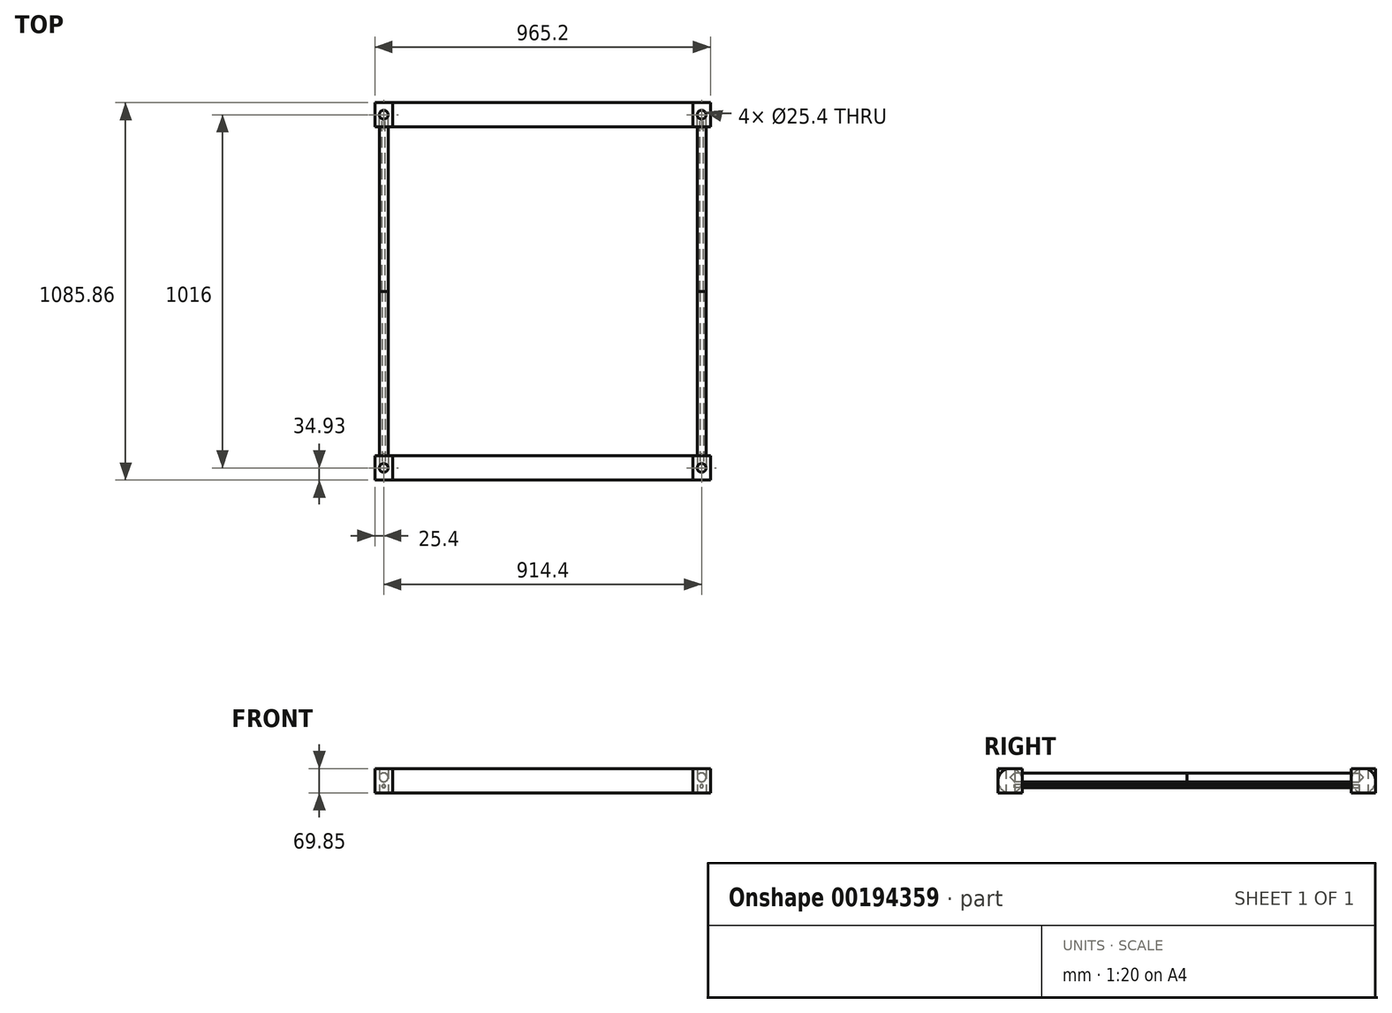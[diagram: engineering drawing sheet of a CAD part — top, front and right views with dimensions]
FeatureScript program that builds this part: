
annotation { "Feature Type Name" : "Feature", "Feature Type Description" : "" }
export const myFeature = defineFeature(function(context is Context, id is Id, definition is map)
    precondition{}
    {
        {
            var Q0;
            Q0=qCreatedBy(makeId("Front.planeOp"),FACE);
            var sketch = newSketch(context, id + "F0", { "sketchPlane" : qUnion([Q0])});
            skCircle(sketch, "E0", {"center": v(-457.2, 0) * mm, "radius": 12.7 * mm});
            skCircle(sketch, "E1", {"center": v(457.2, 0) * mm, "radius": 12.7 * mm});
            skLineSegment(sketch, "E2", {"start": v(-431.8, 25.4) * mm, "end": v(-482.6, 25.4) * mm});
            skLineSegment(sketch, "E3", {"start": v(-482.6, 25.4) * mm, "end": v(-482.6, -44.45) * mm});
            skLineSegment(sketch, "E4", {"start": v(-482.6, -44.45) * mm, "end": v(-431.8, -44.45) * mm});
            skLineSegment(sketch, "E5", {"start": v(482.6, -44.45) * mm, "end": v(482.6, 25.4) * mm});
            skLineSegment(sketch, "E6", {"start": v(482.6, 25.4) * mm, "end": v(431.8, 25.4) * mm});
            skCircle(sketch, "E7", {"center": v(-457.2, -25.4) * mm, "radius": 4.76 * mm});
            skCircle(sketch, "E8", {"center": v(457.2, -25.4) * mm, "radius": 4.76 * mm});
            skLineSegment(sketch, "E9", {"start": v(-431.8, 25.4) * mm, "end": v(-431.8, -44.45) * mm});
            skLineSegment(sketch, "E10", {"start": v(431.8, 25.4) * mm, "end": v(431.8, -44.45) * mm});
            skPoint(sketch, "E10.endSnap0", {"position": v(0, -44.45) * mm});
            skLineSegment(sketch, "E11", {"start": v(-431.8, -9.52) * mm, "end": v(431.8, -9.52) * mm});
            skPoint(sketch, "E12.orphan", {"position": v(0, 25.4) * mm});
            skLineSegment(sketch, "E13.trimOffspring", {"start": v(431.8, -44.45) * mm, "end": v(482.6, -44.45) * mm});
            skLineSegment(sketch, "E14", {"start": v(-431.8, 25.4) * mm, "end": v(431.8, 25.4) * mm});
            skSolve(sketch);
        }
        {
            var Q0;
            Q0=makeQuery(id+"F0.imprint","IMPRINT",FACE,{"disambiguationData":[TD([[makeQuery(id+"F0.imprint","IMPRINT",EDGE,{"derivedFrom":sQuery(id+"F0.wireOp",EDGE,"E1")}),-1.0]])]});
            var Q1;
            Q1=makeQuery(id+"F0.imprint","IMPRINT",FACE,{"disambiguationData":[TD([[makeQuery(id+"F0.imprint","IMPRINT",EDGE,{"derivedFrom":sQuery(id+"F0.wireOp",EDGE,"E0")}),1.0]])]});
            var Q2;
            Q2=makeQuery(id+"F0.imprint","IMPRINT",FACE,{"disambiguationData":[TD([[makeQuery(id+"F0.imprint","IMPRINT",EDGE,{"derivedFrom":sQuery(id+"F0.wireOp",EDGE,"E0")}),-1.0]])]});
            var Q3;
            Q3=makeQuery(id+"F0.imprint","IMPRINT",FACE,{"disambiguationData":[TD([[makeQuery(id+"F0.imprint","IMPRINT",EDGE,{"derivedFrom":sQuery(id+"F0.wireOp",EDGE,"E7")}),1.0]])]});
            var Q4;
            Q4=makeQuery(id+"F0.imprint","IMPRINT",FACE,{"disambiguationData":[TD([[makeQuery(id+"F0.imprint","IMPRINT",EDGE,{"derivedFrom":sQuery(id+"F0.wireOp",EDGE,"E1")}),1.0]])]});
            var Q5;
            Q5=makeQuery(id+"F0.imprint","IMPRINT",FACE,{"disambiguationData":[TD([[makeQuery(id+"F0.imprint","IMPRINT",EDGE,{"derivedFrom":sQuery(id+"F0.wireOp",EDGE,"E8")}),1.0]])]});
            extrude(context, id + "F1", {"entities" : qUnion([Q0, Q1, Q2, Q3, Q4, Q5]), "endBound" : BoundingType.SYMMETRIC, "oppositeDirection" : true, "depth" : 69.85 * mm});
        }
        {
            var Q0;
            {var subQ2=sQuery(id+"F0.wireOp",EDGE,"E11");Q0=makeQuery(id+"F0.imprint","IMPRINT",FACE,{"disambiguationData":[TD([[makeQuery(id+"F0.imprint","IMPRINT",EDGE,{"derivedFrom":subQ2}),1.0]])]});}
            var Q1;
            Q1=sQuery(id+"F0.wireOp",EDGE,"E11");
            revolve(context, id + "F2", {"entities" : qUnion([Q0]), "axis" : qUnion([Q1]), "revolveType" : RevolveType.FULL});
        }
        {
            var Q0;
            Q0=makeQuery(id+"F0.imprint","IMPRINT",FACE,{"disambiguationData":[TD([[makeQuery(id+"F0.imprint","IMPRINT",EDGE,{"derivedFrom":sQuery(id+"F0.wireOp",EDGE,"E1")}),1.0]])]});
            var Q1;
            Q1=makeQuery(id+"F0.imprint","IMPRINT",FACE,{"disambiguationData":[TD([[makeQuery(id+"F0.imprint","IMPRINT",EDGE,{"derivedFrom":sQuery(id+"F0.wireOp",EDGE,"E8")}),1.0]])]});
            var Q2;
            Q2=makeQuery(id+"F0.imprint","IMPRINT",FACE,{"disambiguationData":[TD([[makeQuery(id+"F0.imprint","IMPRINT",EDGE,{"derivedFrom":sQuery(id+"F0.wireOp",EDGE,"E0")}),1.0]])]});
            var Q3;
            Q3=makeQuery(id+"F0.imprint","IMPRINT",FACE,{"disambiguationData":[TD([[makeQuery(id+"F0.imprint","IMPRINT",EDGE,{"derivedFrom":sQuery(id+"F0.wireOp",EDGE,"E7")}),1.0]])]});
            extrude(context, id + "F3", {"entities" : qUnion([Q0, Q1, Q2, Q3]), "oppositeDirection" : true, "depth" : 508 * mm});
        }
        {
            var Q0;
            Q0=qCreatedBy(makeId("Front.planeOp"),FACE);
            cPlane(context, id + "F4", {"entities" : qUnion([Q0]), "cplaneType" : CPlaneType.OFFSET, "offset" : 508 * mm, "oppositeDirection" : true, "width" : 152.4 * mm, "height" : 152.4 * mm});
        }
        {
            var Q0;
            Q0=makeQuery(id+"F2.opRevolve","SWEPT_BODY",BODY,{"disambiguationData":[OSD([sQuery(id+"F0.wireOp",EDGE,"E9"),sQuery(id+"F0.wireOp",EDGE,"E10"),sQuery(id+"F0.wireOp",EDGE,"E11"),sQuery(id+"F0.wireOp",EDGE,"E14")])]});
            var Q1;
            Q1=makeQuery(id+"F1.opExtrude","SWEPT_BODY",BODY,{"disambiguationData":[OSD([sQuery(id+"F0.wireOp",EDGE,"E5"),sQuery(id+"F0.wireOp",EDGE,"E6"),sQuery(id+"F0.wireOp",EDGE,"E10"),sQuery(id+"F0.wireOp",EDGE,"E13.trimOffspring")])]});
            var Q2;
            Q2=makeQuery(id+"F3.opExtrude","SWEPT_BODY",BODY,{"disambiguationData":[OSD([sQuery(id+"F0.wireOp",EDGE,"E1")])]});
            var Q3;
            Q3=makeQuery(id+"F1.opExtrude","SWEPT_BODY",BODY,{"disambiguationData":[OSD([sQuery(id+"F0.wireOp",EDGE,"E2"),sQuery(id+"F0.wireOp",EDGE,"E3"),sQuery(id+"F0.wireOp",EDGE,"E4"),sQuery(id+"F0.wireOp",EDGE,"E9")])]});
            var Q4;
            Q4=makeQuery(id+"F3.opExtrude","SWEPT_BODY",BODY,{"disambiguationData":[OSD([sQuery(id+"F0.wireOp",EDGE,"E0")])]});
            var Q5;
            Q5=makeQuery(id+"F3.opExtrude","SWEPT_BODY",BODY,{"disambiguationData":[OSD([sQuery(id+"F0.wireOp",EDGE,"E7")])]});
            var Q6;
            Q6=makeQuery(id+"F3.opExtrude","SWEPT_BODY",BODY,{"disambiguationData":[OSD([sQuery(id+"F0.wireOp",EDGE,"E8")])]});
            var Q7;
            Q7=qCreatedBy(id+"F4.planeOp",FACE);
            mirror(context, id + "F5", {"entities" : qUnion([Q0, Q1, Q2, Q3, Q4, Q5, Q6]), "mirrorPlane" : qUnion([Q7])});
        }
        {
            var Q0;
            Q0=qCreatedBy(makeId("Top.planeOp"),FACE);
            var sketch = newSketch(context, id + "F6", { "sketchPlane" : qUnion([Q0])});
            skCircle(sketch, "E15", {"center": v(-457.2, 0) * mm, "radius": 12.7 * mm});
            skCircle(sketch, "E16.0.1.0", {"center": v(-457.2, 1016) * mm, "radius": 12.7 * mm});
            skCircle(sketch, "E16.1.0.0", {"center": v(457.2, 0) * mm, "radius": 12.7 * mm});
            skCircle(sketch, "E16.1.1.0", {"center": v(457.2, 1016) * mm, "radius": 12.7 * mm});
            skLineSegment(sketch, "E16.direction1", {"start": v(-457.2, 0) * mm, "end": v(457.2, 0) * mm, "construction": true});
            skLineSegment(sketch, "E16.direction2", {"start": v(-457.2, 0) * mm, "end": v(-457.2, 1016) * mm, "construction": true});
            skSolve(sketch);
        }
        {
            var Q0;
            Q0 = qSketchRegion(id + "F6", true);
            extrude(context, id + "F7", {"entities" : qUnion([Q0]), "operationType" : NewBodyOperationType.REMOVE, "endBound" : BoundingType.SYMMETRIC, "depth" : 127 * mm});
        }
    });
